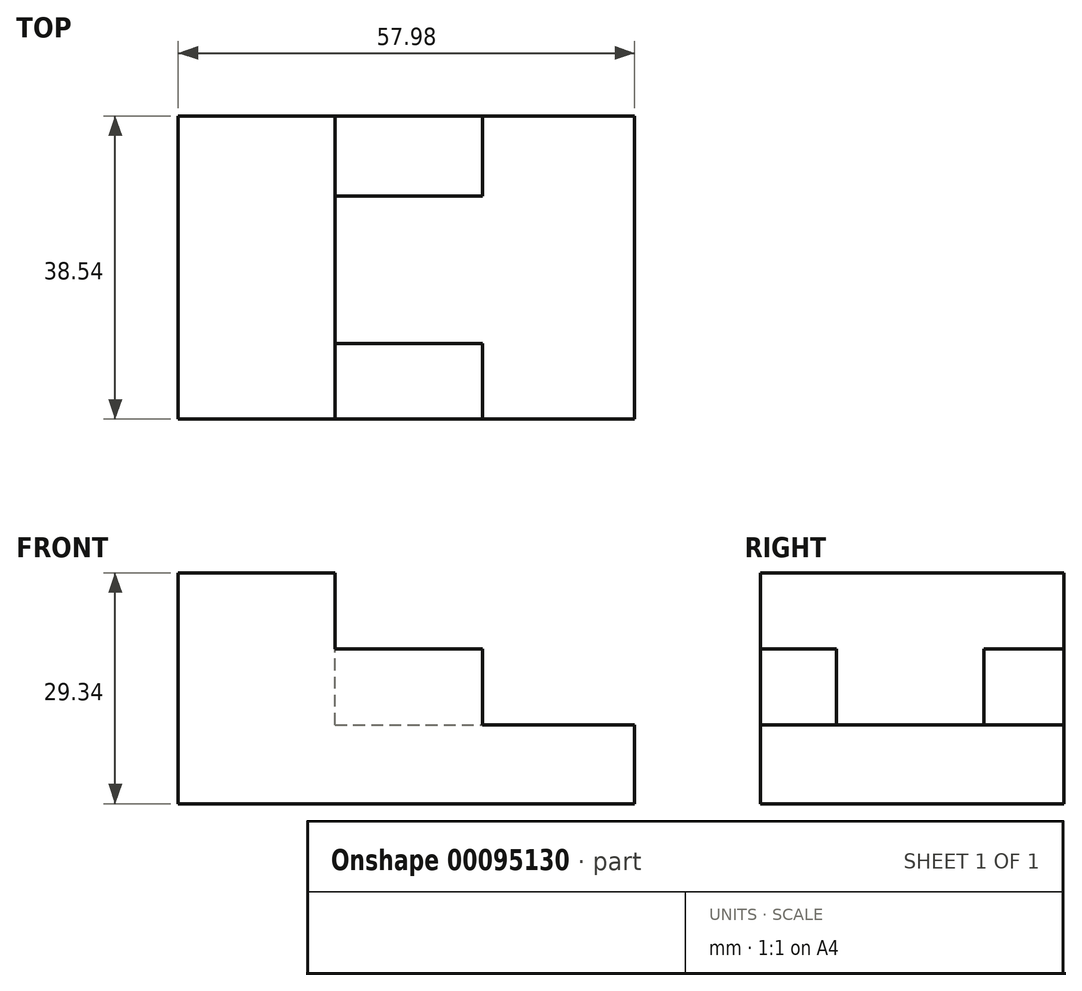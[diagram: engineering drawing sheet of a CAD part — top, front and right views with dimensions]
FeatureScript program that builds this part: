
annotation { "Feature Type Name" : "Feature", "Feature Type Description" : "" }
export const myFeature = defineFeature(function(context is Context, id is Id, definition is map)
    precondition{}
    {
        {
            var Q0;
            Q0=qCreatedBy(makeId("Top.planeOp"),FACE);
            var sketch = newSketch(context, id + "F0", { "sketchPlane" : qUnion([Q0])});
            skLineSegment(sketch, "E0.bottom", {"start": v(-29, 19.27) * mm, "end": v(29, 19.27) * mm});
            skLineSegment(sketch, "E0.top", {"start": v(-29, -19.27) * mm, "end": v(29, -19.27) * mm});
            skLineSegment(sketch, "E0.left", {"start": v(-29, 19.27) * mm, "end": v(-29, -19.27) * mm});
            skLineSegment(sketch, "E0.right", {"start": v(29, 19.27) * mm, "end": v(29, -19.27) * mm});
            skPoint(sketch, "E0.middle", {"position": v(0, 0) * mm});
            skSolve(sketch);
        }
        {
            var Q0;
            Q0 = qSketchRegion(id + "F0", true);
            extrude(context, id + "F1", {"entities" : qUnion([Q0]), "depth" : 10.03 * mm});
        }
        {
            var Q0;
            Q0=makeQuery(id+"F1.opExtrude","CAP_FACE",FACE,{"disambiguationData":[OSD([sQuery(id+"F0.wireOp",EDGE,"E0.bottom"),sQuery(id+"F0.wireOp",EDGE,"E0.top"),sQuery(id+"F0.wireOp",EDGE,"E0.left"),sQuery(id+"F0.wireOp",EDGE,"E0.right")])],"isStart":false});
            var sketch = newSketch(context, id + "F2", { "sketchPlane" : qUnion([Q0])});
            skLineSegment(sketch, "E1.bottom", {"start": v(-29, 19.27) * mm, "end": v(9.7, 19.27) * mm});
            skLineSegment(sketch, "E1.top", {"start": v(-29, -19.27) * mm, "end": v(9.7, -19.27) * mm});
            skLineSegment(sketch, "E1.left", {"start": v(-29, 19.27) * mm, "end": v(-29, -19.27) * mm});
            skLineSegment(sketch, "E1.right", {"start": v(9.7, 19.27) * mm, "end": v(9.7, -19.27) * mm});
            skSolve(sketch);
        }
        {
            var Q0;
            Q0 = qSketchRegion(id + "F2", true);
            extrude(context, id + "F3", {"entities" : qUnion([Q0]), "operationType" : NewBodyOperationType.ADD, "depth" : 9.65 * mm});
        }
        {
            var Q0;
            Q0=makeQuery(id+"F3.opExtrude","CAP_FACE",FACE,{"disambiguationData":[OSD([sQuery(id+"F2.wireOp",EDGE,"E1.bottom"),sQuery(id+"F2.wireOp",EDGE,"E1.top"),sQuery(id+"F2.wireOp",EDGE,"E1.left"),sQuery(id+"F2.wireOp",EDGE,"E1.right")])],"isStart":false});
            var sketch = newSketch(context, id + "F4", { "sketchPlane" : qUnion([Q0])});
            skLineSegment(sketch, "E2.bottom", {"start": v(-9.06, -9.64) * mm, "end": v(9.7, -9.64) * mm});
            skLineSegment(sketch, "E2.top", {"start": v(-9.06, 9.1) * mm, "end": v(9.7, 9.1) * mm});
            skLineSegment(sketch, "E2.left", {"start": v(-9.06, -9.64) * mm, "end": v(-9.06, 9.1) * mm});
            skLineSegment(sketch, "E2.right", {"start": v(9.7, -9.64) * mm, "end": v(9.7, 9.1) * mm});
            skSolve(sketch);
        }
        {
            var Q0;
            Q0 = qSketchRegion(id + "F4", true);
            extrude(context, id + "F5", {"entities" : qUnion([Q0]), "operationType" : NewBodyOperationType.REMOVE, "oppositeDirection" : true, "depth" : 9.65 * mm});
        }
        {
            var Q0;
            Q0=makeQuery(id+"F3.opExtrude","CAP_FACE",FACE,{"disambiguationData":[OSD([sQuery(id+"F2.wireOp",EDGE,"E1.bottom"),sQuery(id+"F2.wireOp",EDGE,"E1.top"),sQuery(id+"F2.wireOp",EDGE,"E1.left"),sQuery(id+"F2.wireOp",EDGE,"E1.right")])],"isStart":false});
            var sketch = newSketch(context, id + "F6", { "sketchPlane" : qUnion([Q0])});
            skLineSegment(sketch, "E3.bottom", {"start": v(-29, -19.27) * mm, "end": v(-9.06, -19.27) * mm});
            skLineSegment(sketch, "E3.top", {"start": v(-29, 19.27) * mm, "end": v(-9.06, 19.27) * mm});
            skLineSegment(sketch, "E3.left", {"start": v(-29, -19.27) * mm, "end": v(-29, 19.27) * mm});
            skLineSegment(sketch, "E3.right", {"start": v(-9.06, -19.27) * mm, "end": v(-9.06, 19.27) * mm});
            skSolve(sketch);
        }
        {
            var Q0;
            Q0 = qSketchRegion(id + "F6", true);
            extrude(context, id + "F7", {"entities" : qUnion([Q0]), "operationType" : NewBodyOperationType.ADD, "depth" : 9.65 * mm});
        }
    });
